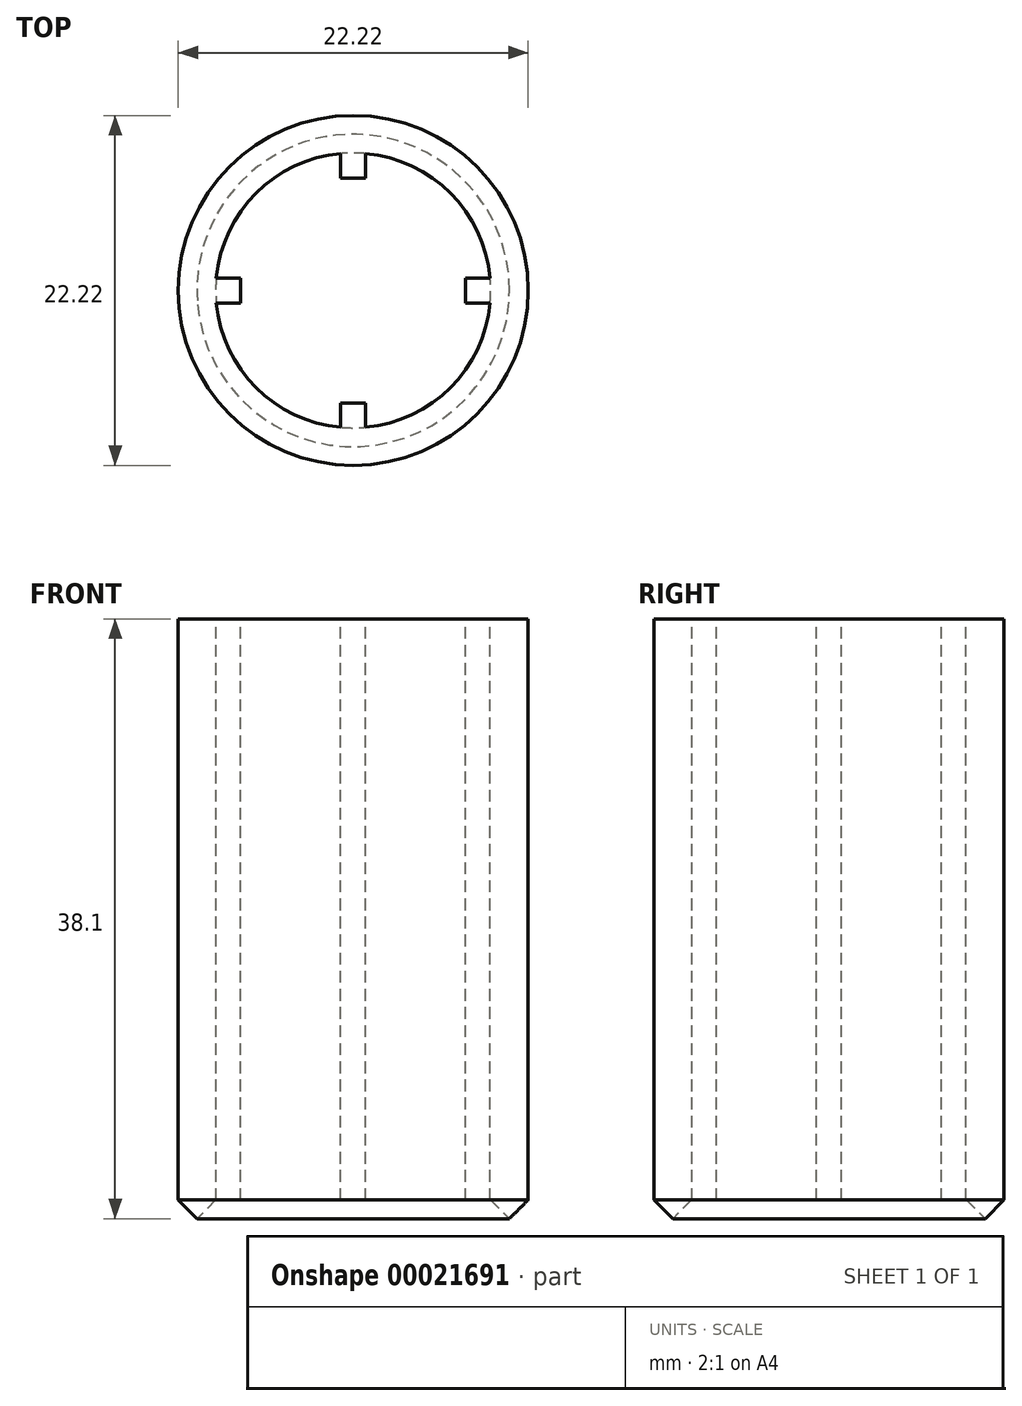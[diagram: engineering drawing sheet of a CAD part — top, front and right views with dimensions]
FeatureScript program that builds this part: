
annotation { "Feature Type Name" : "Feature", "Feature Type Description" : "" }
export const myFeature = defineFeature(function(context is Context, id is Id, definition is map)
    precondition{}
    {
        {
            var Q0;
            Q0=qCreatedBy(makeId("Front.planeOp"),FACE);
            var sketch = newSketch(context, id + "F0", { "sketchPlane" : qUnion([Q0])});
            skLineSegment(sketch, "E0", {"start": v(-8.73, 38.1) * mm, "end": v(-8.73, 1.2) * mm});
            skLineSegment(sketch, "E1", {"start": v(-8.73, 1.2) * mm, "end": v(-9.92, 0) * mm});
            skLineSegment(sketch, "E2", {"start": v(-9.92, 0) * mm, "end": v(-11.11, 1.2) * mm});
            skLineSegment(sketch, "E3", {"start": v(-11.11, 1.2) * mm, "end": v(-11.11, 38.1) * mm});
            skLineSegment(sketch, "E4", {"start": v(-11.11, 38.1) * mm, "end": v(-8.73, 38.1) * mm});
            skLineSegment(sketch, "E5", {"start": v(0, 19.24) * mm, "end": v(0, -5.68) * mm, "construction": true});
            skSolve(sketch);
        }
        {
            var Q0;
            Q0 = qSketchRegion(id + "F0", true);
            var Q1;
            Q1 = qSketchRegion(id + "F2", true);
            var Q2;
            Q2=sQuery(id+"F0.wireOp",EDGE,"E5");
            revolve(context, id + "F1", {"entities" : qUnion([Q0, Q1]), "axis" : qUnion([Q2]), "revolveType" : RevolveType.FULL});
        }
        {
            var Q0;
            Q0=makeQuery(id+"F1.opRevolve","SWEPT_FACE",FACE,{"disambiguationData":[OSD([sQuery(id+"F0.wireOp",EDGE,"E4")])]});
            var sketch = newSketch(context, id + "F2", { "sketchPlane" : qUnion([Q0])});
            skLineSegment(sketch, "E6", {"start": v(-8.73, 0.8) * mm, "end": v(-8.73, -0.8) * mm});
            skLineSegment(sketch, "E7", {"start": v(-8.73, -0.8) * mm, "end": v(-7.14, -0.8) * mm});
            skLineSegment(sketch, "E8", {"start": v(-7.14, -0.8) * mm, "end": v(-7.14, 0.8) * mm});
            skLineSegment(sketch, "E9", {"start": v(-7.14, 0.8) * mm, "end": v(-8.73, 0.8) * mm});
            skLineSegment(sketch, "E10", {"start": v(-0.8, -7.14) * mm, "end": v(-0.8, -8.73) * mm});
            skLineSegment(sketch, "E11", {"start": v(-0.8, -8.73) * mm, "end": v(0.8, -8.73) * mm});
            skLineSegment(sketch, "E12", {"start": v(0.8, -8.73) * mm, "end": v(0.8, -7.14) * mm});
            skLineSegment(sketch, "E13", {"start": v(0.8, -7.14) * mm, "end": v(-0.8, -7.14) * mm});
            skLineSegment(sketch, "E14", {"start": v(7.14, 0.8) * mm, "end": v(7.14, -0.8) * mm});
            skLineSegment(sketch, "E15", {"start": v(7.14, -0.8) * mm, "end": v(8.73, -0.8) * mm});
            skLineSegment(sketch, "E16", {"start": v(8.73, -0.8) * mm, "end": v(8.73, 0.8) * mm});
            skLineSegment(sketch, "E17", {"start": v(8.73, 0.8) * mm, "end": v(7.14, 0.8) * mm});
            skLineSegment(sketch, "E18", {"start": v(-0.8, 8.73) * mm, "end": v(-0.8, 7.14) * mm});
            skLineSegment(sketch, "E19", {"start": v(-0.8, 7.14) * mm, "end": v(0.8, 7.14) * mm});
            skLineSegment(sketch, "E20", {"start": v(0.8, 7.14) * mm, "end": v(0.8, 8.73) * mm});
            skLineSegment(sketch, "E21", {"start": v(0.8, 8.73) * mm, "end": v(-0.8, 8.73) * mm});
            skLineSegment(sketch, "E22", {"start": v(-12.02, 0) * mm, "end": v(12.87, 0) * mm, "construction": true});
            skLineSegment(sketch, "E23", {"start": v(0, 11.48) * mm, "end": v(0, -12.83) * mm, "construction": true});
            skSolve(sketch);
        }
        {
            var Q0;
            Q0 = qSketchRegion(id + "F2", true);
            extrude(context, id + "F3", {"entities" : qUnion([Q0]), "operationType" : NewBodyOperationType.ADD, "oppositeDirection" : true, "depth" : 36.9 * mm});
        }
    });
